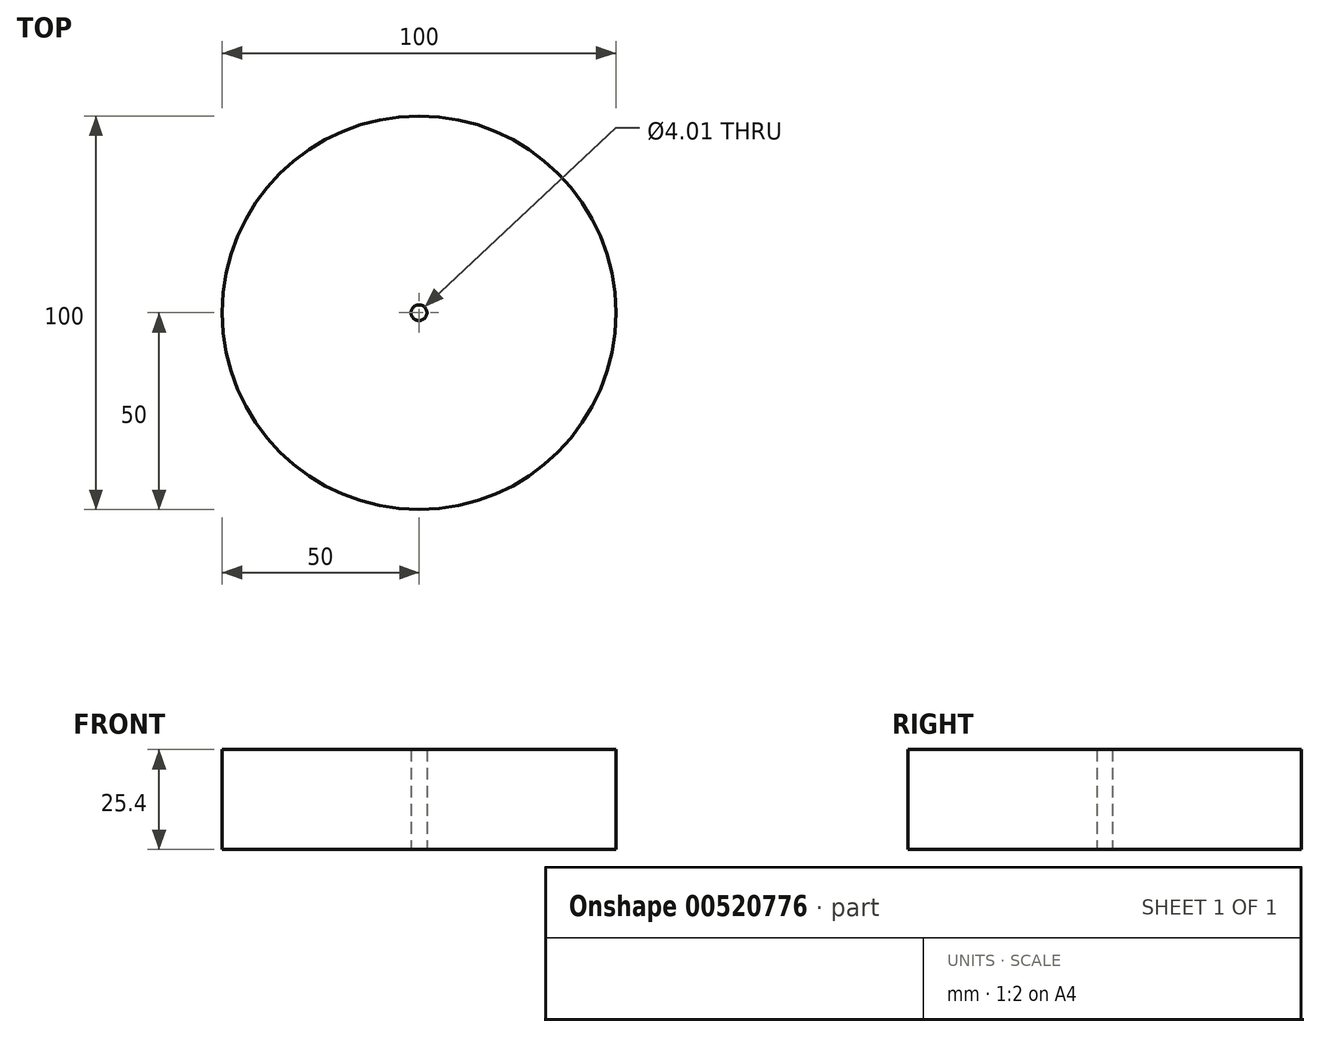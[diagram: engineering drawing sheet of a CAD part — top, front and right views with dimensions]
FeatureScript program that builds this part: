
annotation { "Feature Type Name" : "Feature", "Feature Type Description" : "" }
export const myFeature = defineFeature(function(context is Context, id is Id, definition is map)
    precondition{}
    {
        {
            var Q0;
            Q0=qCreatedBy(makeId("Top.planeOp"),FACE);
            var sketch = newSketch(context, id + "F0", { "sketchPlane" : qUnion([Q0])});
            skCircle(sketch, "E0", {"center": v(0, 0) * mm, "radius": 50 * mm});
            skCircle(sketch, "E1", {"center": v(0, 0) * mm, "radius": 2 * mm});
            skSolve(sketch);
        }
        {
            var Q0;
            Q0=sQuery(id+"F0.wireOp",EDGE,"E1");
            extrude(context, id + "F1", {"bodyType" : ToolBodyType.SURFACE, "surfaceEntities" : qUnion([Q0]), "depth" : 25.4 * mm, "offsetDistance" : 25.4 * mm});
        }
        {
            var Q0;
            Q0 = qSketchRegion(id + "F0", true);
            extrude(context, id + "F2", {"entities" : qUnion([Q0]), "depth" : 25.4 * mm, "offsetDistance" : 25.4 * mm});
        }
    });
